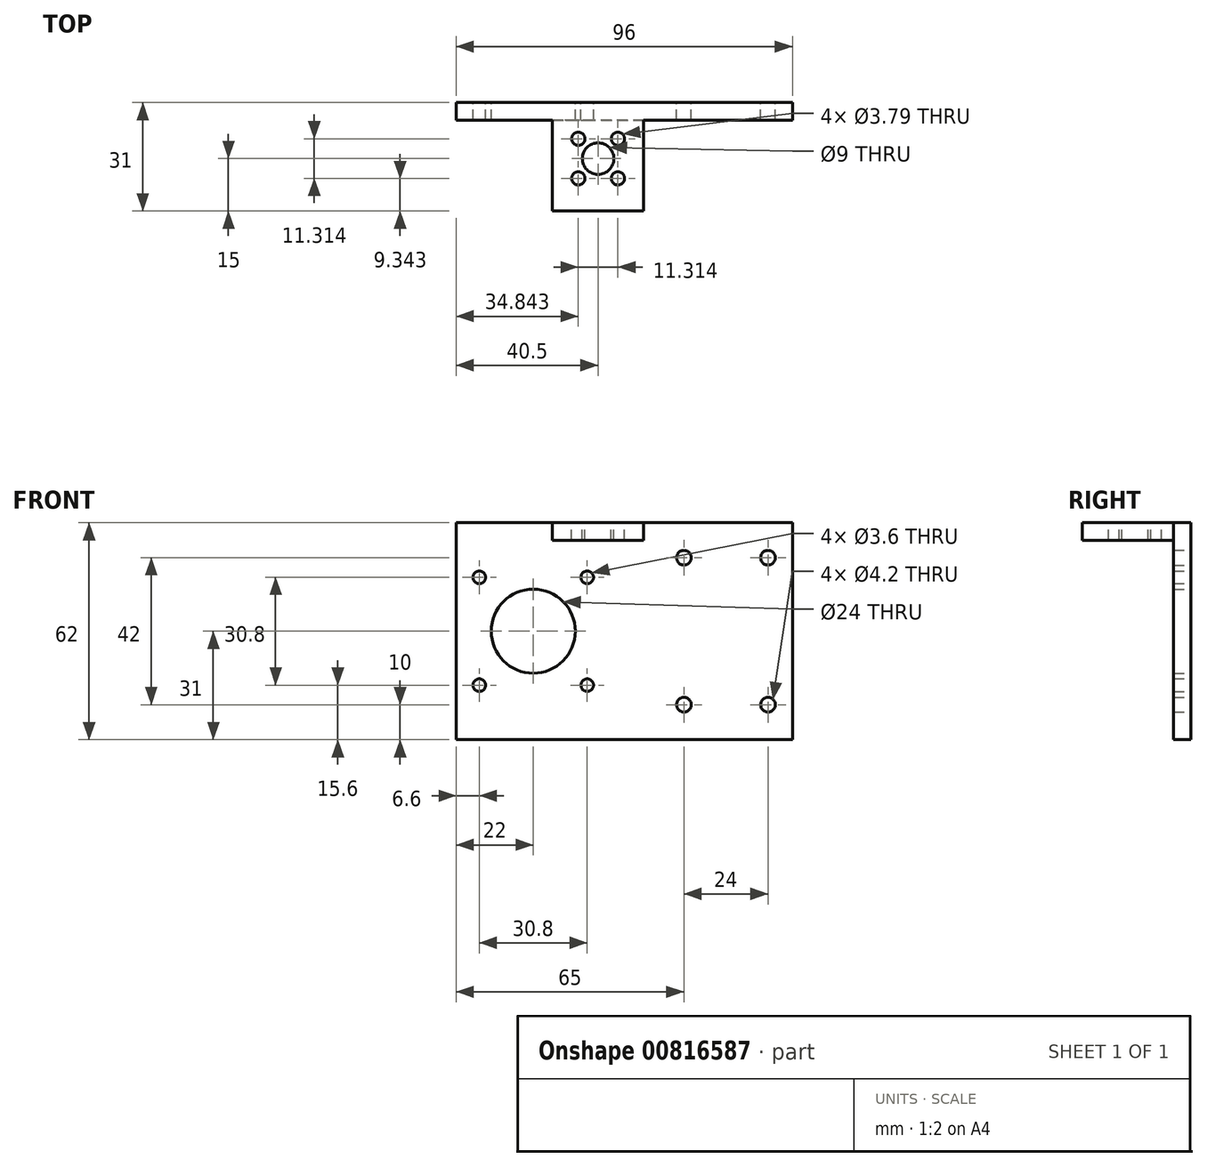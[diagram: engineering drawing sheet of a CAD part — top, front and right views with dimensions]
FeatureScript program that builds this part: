
annotation { "Feature Type Name" : "Feature", "Feature Type Description" : "" }
export const myFeature = defineFeature(function(context is Context, id is Id, definition is map)
    precondition{}
    {
        {
            var Q0;
            Q0=qCreatedBy(makeId("Front.planeOp"),FACE);
            var sketch = newSketch(context, id + "F0", { "sketchPlane" : qUnion([Q0])});
            skLineSegment(sketch, "E0.bottom", {"start": v(-48, 62) * mm, "end": v(48, 62) * mm});
            skLineSegment(sketch, "E0.top", {"start": v(-48, 0) * mm, "end": v(48, 0) * mm});
            skLineSegment(sketch, "E0.left", {"start": v(-48, 62) * mm, "end": v(-48, 0) * mm});
            skLineSegment(sketch, "E0.right", {"start": v(48, 62) * mm, "end": v(48, 0) * mm});
            skCircle(sketch, "E1", {"center": v(-26, 31) * mm, "radius": 12 * mm});
            skCircle(sketch, "E2", {"center": v(-26, 31) * mm, "radius": 21.78 * mm, "construction": true});
            skCircle(sketch, "E3", {"center": v(-41.4, 46.4) * mm, "radius": 1.8 * mm});
            skCircle(sketch, "E4.0.1.0", {"center": v(-41.4, 15.6) * mm, "radius": 1.8 * mm});
            skCircle(sketch, "E4.1.0.0", {"center": v(-10.6, 46.4) * mm, "radius": 1.8 * mm});
            skCircle(sketch, "E4.1.1.0", {"center": v(-10.6, 15.6) * mm, "radius": 1.8 * mm});
            skLineSegment(sketch, "E4.direction1", {"start": v(-41.4, 46.4) * mm, "end": v(-10.6, 46.4) * mm, "construction": true});
            skLineSegment(sketch, "E4.direction2", {"start": v(-41.4, 46.4) * mm, "end": v(-41.4, 15.6) * mm, "construction": true});
            skCircle(sketch, "E5", {"center": v(17, 52) * mm, "radius": 2.1 * mm});
            skCircle(sketch, "E6.0.1.0", {"center": v(17, 10) * mm, "radius": 2.1 * mm});
            skCircle(sketch, "E6.1.0.0", {"center": v(41, 52) * mm, "radius": 2.1 * mm});
            skCircle(sketch, "E6.1.1.0", {"center": v(41, 10) * mm, "radius": 2.1 * mm});
            skLineSegment(sketch, "E6.direction1", {"start": v(17, 52) * mm, "end": v(41, 52) * mm, "construction": true});
            skLineSegment(sketch, "E6.direction2", {"start": v(17, 52) * mm, "end": v(17, 10) * mm, "construction": true});
            skLineSegment(sketch, "E7", {"start": v(48, 31) * mm, "end": v(-48, 31) * mm, "construction": true});
            skLineSegment(sketch, "E8", {"start": v(10, 62) * mm, "end": v(10, 0) * mm, "construction": true});
            skLineSegment(sketch, "E9", {"start": v(29, 52) * mm, "end": v(29, 31) * mm, "construction": true});
            skSolve(sketch);
        }
        {
            var Q0;
            {var subQ5=sQuery(id+"F0.wireOp",EDGE,"E0.bottom");Q0=makeQuery(id+"F0.imprint","IMPRINT",FACE,{"disambiguationData":[TD([[makeQuery(id+"F0.imprint","IMPRINT",EDGE,{"derivedFrom":subQ5}),-1.0]])]});}
            var Q1;
            {var subQ0=sQuery(id+"F0.wireOp",EDGE,"NZwpmoun-o7Oo-fUlM-noFk-b5d9csOMFY5G");Q1=makeQuery(id+"F0.imprint","IMPRINT",FACE,{"disambiguationData":[TD([[makeQuery(id+"F0.imprint","IMPRINT",EDGE,{"derivedFrom":subQ0}),-1.0]])]});}
            extrude(context, id + "F1", {"entities" : qUnion([Q0, Q1]), "depth" : 5 * mm, "offsetDistance" : 25 * mm});
        }
        {
            var Q0;
            Q0=makeQuery(id+"F1.opExtrude","CAP_FACE",FACE,{"disambiguationData":[OSD([sQuery(id+"F0.wireOp",EDGE,"E0.bottom"),sQuery(id+"F0.wireOp",EDGE,"E0.top"),sQuery(id+"F0.wireOp",EDGE,"E0.left"),sQuery(id+"F0.wireOp",EDGE,"E0.right"),sQuery(id+"F0.wireOp",EDGE,"E1"),sQuery(id+"F0.wireOp",EDGE,"E3"),sQuery(id+"F0.wireOp",EDGE,"E4.0.1.0"),sQuery(id+"F0.wireOp",EDGE,"E4.1.0.0"),sQuery(id+"F0.wireOp",EDGE,"E4.1.1.0"),sQuery(id+"F0.wireOp",EDGE,"E5"),sQuery(id+"F0.wireOp",EDGE,"E6.0.1.0"),sQuery(id+"F0.wireOp",EDGE,"E6.1.0.0"),sQuery(id+"F0.wireOp",EDGE,"E6.1.1.0")])],"isStart":false});
            var sketch = newSketch(context, id + "F2", { "sketchPlane" : qUnion([Q0])});
            skLineSegment(sketch, "E10.bottom", {"start": v(5.5, 62) * mm, "end": v(-20.5, 62) * mm});
            skLineSegment(sketch, "E10.top", {"start": v(5.5, 57) * mm, "end": v(-20.5, 57) * mm});
            skLineSegment(sketch, "E10.left", {"start": v(5.5, 62) * mm, "end": v(5.5, 57) * mm});
            skLineSegment(sketch, "E10.right", {"start": v(-20.5, 62) * mm, "end": v(-20.5, 57) * mm});
            skLineSegment(sketch, "E11", {"start": v(-7.5, 57) * mm, "end": v(-7.5, 62) * mm, "construction": true});
            skLineSegment(sketch, "E12.bottom", {"start": v(-11.5, 57) * mm, "end": v(-3.5, 57) * mm, "construction": true});
            skLineSegment(sketch, "E12.top", {"start": v(-11.5, 62) * mm, "end": v(-3.5, 62) * mm, "construction": true});
            skLineSegment(sketch, "E12.left", {"start": v(-11.5, 57) * mm, "end": v(-11.5, 62) * mm, "construction": true});
            skLineSegment(sketch, "E12.right", {"start": v(-3.5, 57) * mm, "end": v(-3.5, 62) * mm, "construction": true});
            skSolve(sketch);
        }
        {
            var Q0;
            Q0=makeQuery(id+"F2.imprint","IMPRINT",FACE,{"disambiguationData":[TD([[makeQuery(id+"F2.imprint","IMPRINT",EDGE,{"derivedFrom":sQuery(id+"F2.wireOp",EDGE,"E10.bottom")}),-1.0]])]});
            extrude(context, id + "F3", {"entities" : qUnion([Q0]), "operationType" : NewBodyOperationType.ADD, "depth" : 26 * mm, "offsetDistance" : 25 * mm});
        }
        {
            var Q0;
            Q0=makeQuery(id+"F3.boolean.opBoolean","MERGE",FACE,{"derivedFrom":[makeQuery(id+"F1.opExtrude","SWEPT_FACE",FACE,{"disambiguationData":[OSD([sQuery(id+"F0.wireOp",EDGE,"E0.bottom")])]}),makeQuery(id+"F3.opExtrude","SWEPT_FACE",FACE,{"disambiguationData":[OSD([sQuery(id+"F2.wireOp",EDGE,"E10.bottom")])]})]});
            var sketch = newSketch(context, id + "F4", { "sketchPlane" : qUnion([Q0])});
            skLineSegment(sketch, "E13", {"start": v(-20.5, -16) * mm, "end": v(5.5, -16) * mm, "construction": true});
            skCircle(sketch, "E14", {"center": v(-7.5, -16) * mm, "radius": 4.5 * mm});
            skCircle(sketch, "E15", {"center": v(-7.5, -16) * mm, "radius": 8 * mm, "construction": true});
            skCircle(sketch, "E16", {"center": v(-13.16, -10.34) * mm, "radius": 1.9 * mm});
            skCircle(sketch, "E17.1.0", {"center": v(-13.16, -21.66) * mm, "radius": 1.9 * mm});
            skCircle(sketch, "E17.2.0", {"center": v(-1.84, -21.66) * mm, "radius": 1.9 * mm});
            skCircle(sketch, "E17.3.0", {"center": v(-1.84, -10.34) * mm, "radius": 1.9 * mm});
            skLineSegment(sketch, "E18", {"start": v(-13.16, -10.34) * mm, "end": v(-1.84, -10.34) * mm, "construction": true});
            skSolve(sketch);
        }
        {
            var Q0;
            Q0=makeQuery(id+"F4.imprint","IMPRINT",FACE,{"disambiguationData":[TD([[makeQuery(id+"F4.imprint","IMPRINT",EDGE,{"derivedFrom":sQuery(id+"F4.wireOp",EDGE,"E14")}),1.0]])]});
            var Q1;
            Q1=makeQuery(id+"F4.imprint","IMPRINT",FACE,{"disambiguationData":[TD([[makeQuery(id+"F4.imprint","IMPRINT",EDGE,{"derivedFrom":sQuery(id+"F4.wireOp",EDGE,"E16")}),1.0]])]});
            var Q2;
            Q2=makeQuery(id+"F4.imprint","IMPRINT",FACE,{"disambiguationData":[TD([[makeQuery(id+"F4.imprint","IMPRINT",EDGE,{"derivedFrom":sQuery(id+"F4.wireOp",EDGE,"E17.3.0")}),1.0]])]});
            var Q3;
            Q3=makeQuery(id+"F4.imprint","IMPRINT",FACE,{"disambiguationData":[TD([[makeQuery(id+"F4.imprint","IMPRINT",EDGE,{"derivedFrom":sQuery(id+"F4.wireOp",EDGE,"E17.2.0")}),1.0]])]});
            var Q4;
            Q4=makeQuery(id+"F4.imprint","IMPRINT",FACE,{"disambiguationData":[TD([[makeQuery(id+"F4.imprint","IMPRINT",EDGE,{"derivedFrom":sQuery(id+"F4.wireOp",EDGE,"E17.1.0")}),1.0]])]});
            extrude(context, id + "F5", {"entities" : qUnion([Q0, Q1, Q2, Q3, Q4]), "operationType" : NewBodyOperationType.REMOVE, "oppositeDirection" : true, "depth" : 25 * mm, "offsetDistance" : 25 * mm});
        }
    });
